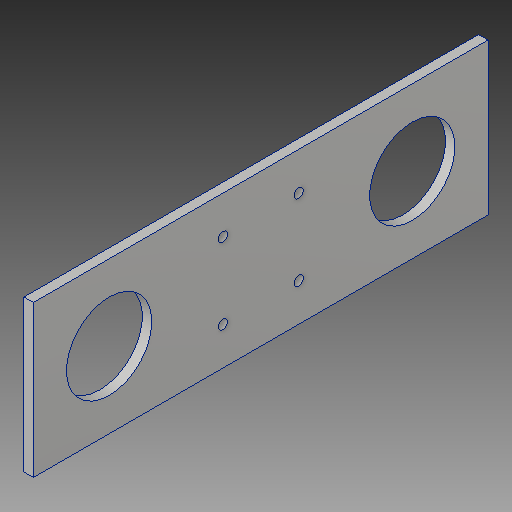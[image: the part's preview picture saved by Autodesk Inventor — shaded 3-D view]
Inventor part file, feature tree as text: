
AUTODESK INVENTOR PART (.ipt)
format: ipt  version: 2017 (Build 210142000, 142)  size: 110,080 bytes
history: native  units: in
note: dims shown in document units (in); Inventor stores cm internally (conversion verified against a paired STEP export)
features: extrude x1, sketch x1
ambient origin geometry x8: Origin, YZ Plane, XZ Plane, XY Plane, X Axis, Y Axis, Z Axis, Center Point
bodies: Body1 (feature_tree)
feature tree (2):
  extrude  "Extrusion2"  Depth=6.0in
  sketch  "Sketch1"  dims[d11=2.0in d12=6.0in d13=1.0in d14=1.125in d22=0.5in d23=0.5in d24=0.125in d25=0.125in d26=0.0in]
